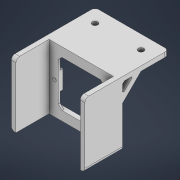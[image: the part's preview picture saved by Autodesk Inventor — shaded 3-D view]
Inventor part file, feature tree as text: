
AUTODESK INVENTOR PART (.ipt)
format: ipt  version: 2021 (Build 250183000, 183)  size: 228,864 bytes
history: native  units: mm
features: sketch x8, extrude x6, mirror x3, hole x2, fillet x2, chamfer x2, plane x1
ambient origin geometry x8: Origin, YZ Plane, XZ Plane, XY Plane, X Axis, Y Axis, Z Axis, Center Point
bodies: Solid1 (feature_tree)
feature tree (24):
  extrude  "Extrusion1"  Depth=40.0mm
  extrude  "Extrusion2"  Depth=25.0mm
  hole  "Hole1"  [1 undecoded]
  extrude  "Extrusion3"  Depth=2.5mm
  fillet  "Fillet1"  Radius=25.0mm
  chamfer  "Chamfer1"  Distance=2.0mm Angle=45.0deg
  extrude  "Extrusion4"  Depth=10.0mm
  plane  "Work Plane1"
  mirror  "Mirror1"
  hole  "Hole2"  [1 undecoded]
  chamfer  "Chamfer2"  Distance=7.5mm
  extrude  "Extrusion5"  Depth=1.0mm TaperAngle=45.0deg
  mirror  "Mirror2"
  extrude  "Extrusion6"  Depth=2.0mm
  fillet  "Fillet2"  Radius=10.0mm
  mirror  "Mirror3"
  sketch  "Sketch1"  dims[d0=35.0mm d1=40.0mm]
  sketch  "Sketch2"  dims[d2=2.5mm d3=0.0mm d4=25.0mm]
  sketch  "Sketch3"  dims[d5=5.0mm d6=0.0mm d7=29.0mm]
  sketch  "Sketch4"  dims[d8=2.0mm d9=6.0mm d10=4.0mm d11=2.0mm d12=90.0deg d13=8.0mm d14=20.594885mm d15=2.5mm d16=25.0mm d17=0.0mm]
  sketch  "Sketch5"  dims[d18=2.0mm d19=2.0mm d20=2.0mm d21=45.0deg]
  sketch  "Sketch6"  dims[d22=10.0mm d23=10.0mm]
  sketch  "Sketch7"  dims[d24=3.0mm d25=3.0mm d26=0.0mm]
  sketch  "Sketch8"  dims[d27=25.0mm d28=7.5mm d29=3.0mm d30=6.0mm d31=4.0mm d32=2.0mm d33=90.0deg d34=8.0mm d35=20.594885mm d36=1.0mm d37=2.0mm d38=45.0deg d39=6.0mm d40=10.0mm d41=1.5mm d42=0.0mm d43=0.5mm d44=18.0mm d45=0.0mm d46=2.0mm]
note: 2 required parameter values undecoded (feature->parameter linkage not recoverable at this tier; creation-order binding heuristic only, values carry confidence <= 0.55)
